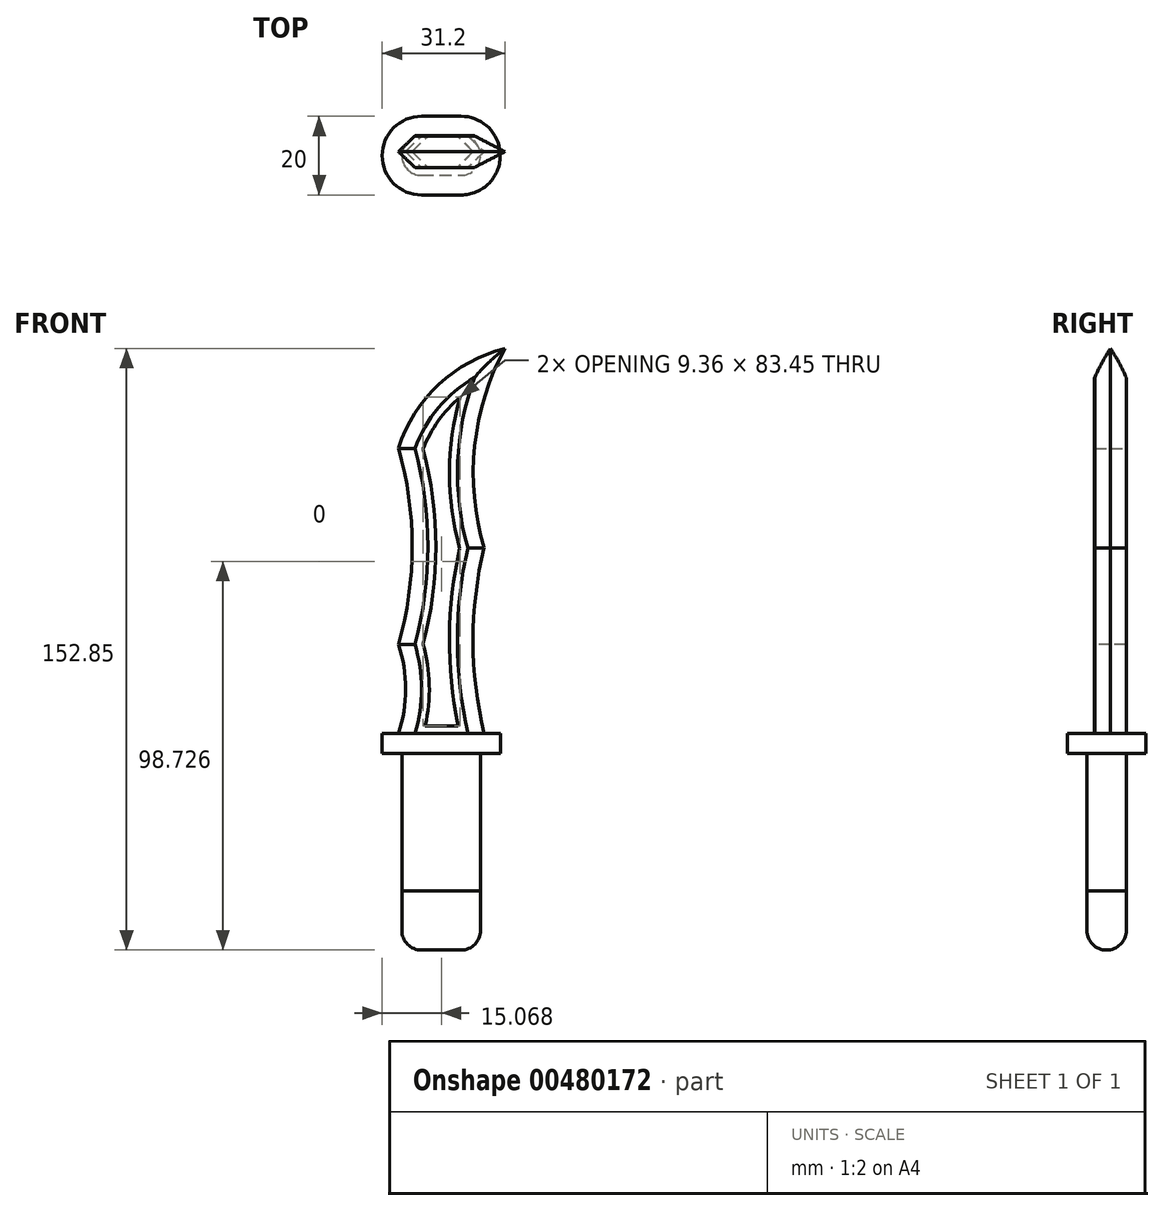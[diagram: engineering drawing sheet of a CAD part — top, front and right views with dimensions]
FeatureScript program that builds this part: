
annotation { "Feature Type Name" : "Feature", "Feature Type Description" : "" }
export const myFeature = defineFeature(function(context is Context, id is Id, definition is map)
    precondition{}
    {
        {
            var Q0;
            Q0=qCreatedBy(makeId("Front.planeOp"),FACE);
            var sketch = newSketch(context, id + "F0", { "sketchPlane" : qUnion([Q0])});
            skLineSegment(sketch, "E0.bottom", {"start": v(-9.92, 0) * mm, "end": v(10.08, 0) * mm});
            skLineSegment(sketch, "E0.top", {"start": v(-9.92, -50) * mm, "end": v(10.08, -50) * mm});
            skLineSegment(sketch, "E0.left", {"start": v(-9.92, 0) * mm, "end": v(-9.92, -50) * mm});
            skLineSegment(sketch, "E0.right", {"start": v(10.08, 0) * mm, "end": v(10.08, -50) * mm});
            skLineSegment(sketch, "E1", {"start": v(-9.92, -35) * mm, "end": v(10.08, -35) * mm});
            skLineSegment(sketch, "E2", {"start": v(-47.28, 5) * mm, "end": v(68.13, 5) * mm});
            skPoint(sketch, "E3", {"position": v(-9.92, 5) * mm});
            skPoint(sketch, "E4", {"position": v(10.08, 5) * mm});
            skPoint(sketch, "E5", {"position": v(14.08, 5) * mm});
            skPoint(sketch, "E6", {"position": v(-13.92, 5) * mm});
            skArc(sketch, "E7", {"start": v(14.08, 52.31) * mm, "mid": v(11.16, 28.66) * mm, "end": v(14.08, 5) * mm});
            skArc(sketch, "E8", {"start": v(22.24, 106.85) * mm, "mid": v(11.9, 80.52) * mm, "end": v(14.08, 52.31) * mm});
            skArc(sketch, "E9", {"start": v(-13.92, 5) * mm, "mid": v(-11.95, 16.28) * mm, "end": v(-13.92, 27.57) * mm});
            skArc(sketch, "E10", {"start": v(-13.92, 27.57) * mm, "mid": v(-10.3, 52.54) * mm, "end": v(-13.92, 77.52) * mm});
            skArc(sketch, "E11", {"start": v(22.24, 106.85) * mm, "mid": v(-0.4, 97.8) * mm, "end": v(-13.92, 77.52) * mm});
            skSolve(sketch);
        }
        {
            var Q0;
            {var subQ0=sQuery(id+"F0.wireOp",EDGE,"E0.bottom");Q0=makeQuery(id+"F0.imprint","IMPRINT",FACE,{"disambiguationData":[TD([[makeQuery(id+"F0.imprint","IMPRINT",EDGE,{"derivedFrom":subQ0}),-1.0]])]});}
            extrude(context, id + "F1", {"entities" : qUnion([Q0]), "depth" : 10 * mm});
        }
        {
            var Q0;
            {var subQ0=sQuery(id+"F0.wireOp",EDGE,"E0.top");Q0=makeQuery(id+"F0.imprint","IMPRINT",FACE,{"disambiguationData":[TD([[makeQuery(id+"F0.imprint","IMPRINT",EDGE,{"derivedFrom":subQ0}),1.0]])]});}
            extrude(context, id + "F2", {"entities" : qUnion([Q0]), "depth" : 10 * mm});
        }
        {
            var Q0;
            Q0=makeQuery(id+"F1.opExtrude","CAP_EDGE",EDGE,{"disambiguationData":[OSD([sQuery(id+"F0.wireOp",EDGE,"E0.right")])],"isStart":false});
            var Q1;
            Q1=makeQuery(id+"F2.opExtrude","CAP_EDGE",EDGE,{"disambiguationData":[OSD([sQuery(id+"F0.wireOp",EDGE,"E0.right")])],"isStart":false});
            var Q2;
            Q2=makeQuery(id+"F1.opExtrude","CAP_EDGE",EDGE,{"disambiguationData":[OSD([sQuery(id+"F0.wireOp",EDGE,"E0.right")])],"isStart":true});
            var Q3;
            Q3=makeQuery(id+"F2.opExtrude","CAP_EDGE",EDGE,{"disambiguationData":[OSD([sQuery(id+"F0.wireOp",EDGE,"E0.right")])],"isStart":true});
            var Q4;
            Q4=makeQuery(id+"F2.opExtrude","CAP_EDGE",EDGE,{"disambiguationData":[OSD([sQuery(id+"F0.wireOp",EDGE,"E0.left")])],"isStart":true});
            var Q5;
            Q5=makeQuery(id+"F1.opExtrude","CAP_EDGE",EDGE,{"disambiguationData":[OSD([sQuery(id+"F0.wireOp",EDGE,"E0.left")])],"isStart":true});
            var Q6;
            Q6=makeQuery(id+"F1.opExtrude","CAP_EDGE",EDGE,{"disambiguationData":[OSD([sQuery(id+"F0.wireOp",EDGE,"E0.left")])],"isStart":false});
            var Q7;
            Q7=makeQuery(id+"F2.opExtrude","CAP_EDGE",EDGE,{"disambiguationData":[OSD([sQuery(id+"F0.wireOp",EDGE,"E0.left")])],"isStart":false});
            var Q8;
            Q8=makeQuery(id+"F2.opExtrude","CAP_EDGE",EDGE,{"disambiguationData":[OSD([sQuery(id+"F0.wireOp",EDGE,"E0.top")])],"isStart":false});
            var Q9;
            Q9=makeQuery(id+"F2.opExtrude","SWEPT_EDGE",EDGE,{"disambiguationData":[OSD([sQuery(id+"F0.wireOp",EDGE,"E0.top"),sQuery(id+"F0.wireOp",EDGE,"E0.left")])]});
            var Q10;
            Q10=makeQuery(id+"F2.opExtrude","CAP_EDGE",EDGE,{"disambiguationData":[OSD([sQuery(id+"F0.wireOp",EDGE,"E0.top")])],"isStart":true});
            var Q11;
            Q11=makeQuery(id+"F2.opExtrude","SWEPT_EDGE",EDGE,{"disambiguationData":[OSD([sQuery(id+"F0.wireOp",EDGE,"E0.top"),sQuery(id+"F0.wireOp",EDGE,"E0.right")])]});
            fillet(context, id + "F3", {"entities" : qUnion([Q0, Q1, Q2, Q3, Q4, Q5, Q6, Q7, Q8, Q9, Q10, Q11]), "radius" : 5 * mm, "tangentPropagation" : true, "allowEdgeOverflow" : false});
        }
        {
            var Q0;
            Q0=qCreatedBy(makeId("Top.planeOp"),FACE);
            var sketch = newSketch(context, id + "F4", { "sketchPlane" : qUnion([Q0])});
            skArc(sketch, "E12.0", {"start": v(5.08, -15) * mm, "mid": v(15.08, -5) * mm, "end": v(5.08, 5) * mm});
            skLineSegment(sketch, "E12.1", {"start": v(-4.92, -15) * mm, "end": v(5.08, -15) * mm});
            skArc(sketch, "E12.2", {"start": v(-4.92, 5) * mm, "mid": v(-14.92, -5) * mm, "end": v(-4.92, -15) * mm});
            skLineSegment(sketch, "E12.3", {"start": v(5.08, 5) * mm, "end": v(-4.92, 5) * mm});
            skSolve(sketch);
        }
        {
            var Q0;
            Q0=makeQuery(id+"F4.imprint","IMPRINT",FACE,{"disambiguationData":[TD([[makeQuery(id+"F4.imprint","IMPRINT",EDGE,{"derivedFrom":sQuery(id+"F4.wireOp",EDGE,"E12.0")}),1.0]])]});
            extrude(context, id + "F5", {"entities" : qUnion([Q0]), "depth" : 5 * mm});
        }
        {
            var Q0;
            {var subQ1=sQuery(id+"F0.wireOp",EDGE,"E7");Q0=makeQuery(id+"F0.imprint","IMPRINT",FACE,{"disambiguationData":[TD([[makeQuery(id+"F0.imprint","IMPRINT",EDGE,{"derivedFrom":subQ1}),-1.0]])]});}
            extrude(context, id + "F6", {"entities" : qUnion([Q0]), "depth" : 8 * mm});
        }
        {
            var Q0;
            Q0=makeQuery(id+"F6.opExtrude","CAP_EDGE",EDGE,{"disambiguationData":[OSD([sQuery(id+"F0.wireOp",EDGE,"E8")])],"isStart":false});
            var Q1;
            Q1=makeQuery(id+"F6.opExtrude","CAP_EDGE",EDGE,{"disambiguationData":[OSD([sQuery(id+"F0.wireOp",EDGE,"E7")])],"isStart":false});
            chamfer(context, id + "F7", {"entities" : qUnion([Q0, Q1]), "width" : 7 * mm, "tangentPropagation" : true});
        }
        {
            var Q0;
            Q0=makeQuery(id+"F6.opExtrude","CAP_EDGE",EDGE,{"disambiguationData":[OSD([sQuery(id+"F0.wireOp",EDGE,"E8")])],"isStart":true});
            var Q1;
            Q1=makeQuery(id+"F6.opExtrude","CAP_EDGE",EDGE,{"disambiguationData":[OSD([sQuery(id+"F0.wireOp",EDGE,"E7")])],"isStart":true});
            chamfer(context, id + "F8", {"entities" : qUnion([Q0, Q1]), "width" : 7 * mm, "tangentPropagation" : true});
        }
        {
            var Q0;
            Q0=makeQuery(id+"F6.opExtrude","CAP_EDGE",EDGE,{"disambiguationData":[OSD([sQuery(id+"F0.wireOp",EDGE,"E11")])],"isStart":true});
            var Q1;
            Q1=makeQuery(id+"F6.opExtrude","CAP_EDGE",EDGE,{"disambiguationData":[OSD([sQuery(id+"F0.wireOp",EDGE,"E10")])],"isStart":true});
            var Q2;
            Q2=makeQuery(id+"F6.opExtrude","CAP_EDGE",EDGE,{"disambiguationData":[OSD([sQuery(id+"F0.wireOp",EDGE,"E9")])],"isStart":true});
            chamfer(context, id + "F9", {"entities" : qUnion([Q0, Q1, Q2]), "width" : 7 * mm, "tangentPropagation" : true});
        }
        {
            var Q0;
            Q0=makeQuery(id+"F6.opExtrude","CAP_EDGE",EDGE,{"disambiguationData":[OSD([sQuery(id+"F0.wireOp",EDGE,"E9")])],"isStart":false});
            var Q1;
            Q1=makeQuery(id+"F6.opExtrude","CAP_EDGE",EDGE,{"disambiguationData":[OSD([sQuery(id+"F0.wireOp",EDGE,"E10")])],"isStart":false});
            var Q2;
            Q2=makeQuery(id+"F6.opExtrude","CAP_EDGE",EDGE,{"disambiguationData":[OSD([sQuery(id+"F0.wireOp",EDGE,"E11")])],"isStart":false});
            chamfer(context, id + "F10", {"entities" : qUnion([Q0, Q1, Q2]), "width" : 7 * mm, "tangentPropagation" : true});
        }
        {
            var Q0;
            Q0=makeQuery(id+"F6.opExtrude","CAP_FACE",FACE,{"disambiguationData":[OSD([sQuery(id+"F0.wireOp",EDGE,"E2"),sQuery(id+"F0.wireOp",EDGE,"E7"),sQuery(id+"F0.wireOp",EDGE,"E8"),sQuery(id+"F0.wireOp",EDGE,"E9"),sQuery(id+"F0.wireOp",EDGE,"E10"),sQuery(id+"F0.wireOp",EDGE,"E11")])],"isStart":false});
            var sketch = newSketch(context, id + "F11", { "sketchPlane" : qUnion([Q0])});
            skArc(sketch, "E13.0", {"start": v(4.39, 7) * mm, "mid": v(2.16, 29.56) * mm, "end": v(4.77, 52.08) * mm});
            skArc(sketch, "E13.1", {"start": v(4.83, 90.45) * mm, "mid": v(-0.69, 84.47) * mm, "end": v(-4.51, 77.29) * mm});
            skArc(sketch, "E13.2", {"start": v(-4.51, 77.29) * mm, "mid": v(-1.3, 52.5) * mm, "end": v(-4.53, 27.73) * mm});
            skArc(sketch, "E13.3", {"start": v(4.77, 52.08) * mm, "mid": v(2.2, 71.27) * mm, "end": v(4.83, 90.45) * mm});
            skArc(sketch, "E13.4", {"start": v(-4.53, 27.73) * mm, "mid": v(-2.96, 17.4) * mm, "end": v(-3.98, 7) * mm});
            skLineSegment(sketch, "E13.5", {"start": v(-3.98, 7) * mm, "end": v(4.39, 7) * mm});
            skSolve(sketch);
        }
        {
            var Q0;
            Q0=makeQuery(id+"F11.imprint","IMPRINT",FACE,{"disambiguationData":[TD([[makeQuery(id+"F11.imprint","IMPRINT",EDGE,{"derivedFrom":sQuery(id+"F11.wireOp",EDGE,"E13.0")}),1.0]])]});
            extrude(context, id + "F12", {"entities" : qUnion([Q0]), "depth" : 0.05 * mm, "offsetDistance" : 25 * mm});
        }
        {
            var Q0;
            Q0=makeQuery(id+"F6.opExtrude","CAP_FACE",FACE,{"disambiguationData":[OSD([sQuery(id+"F0.wireOp",EDGE,"E2"),sQuery(id+"F0.wireOp",EDGE,"E7"),sQuery(id+"F0.wireOp",EDGE,"E8"),sQuery(id+"F0.wireOp",EDGE,"E9"),sQuery(id+"F0.wireOp",EDGE,"E10"),sQuery(id+"F0.wireOp",EDGE,"E11")])],"isStart":true});
            var sketch = newSketch(context, id + "F13", { "sketchPlane" : qUnion([Q0])});
            skArc(sketch, "E14.0", {"start": v(-4.77, 52.08) * mm, "mid": v(-2.16, 29.56) * mm, "end": v(-4.39, 7) * mm});
            skArc(sketch, "E14.1", {"start": v(3.98, 7) * mm, "mid": v(2.96, 17.4) * mm, "end": v(4.53, 27.73) * mm});
            skArc(sketch, "E14.2", {"start": v(4.53, 27.73) * mm, "mid": v(1.3, 52.5) * mm, "end": v(4.51, 77.29) * mm});
            skLineSegment(sketch, "E14.3", {"start": v(-4.39, 7) * mm, "end": v(3.98, 7) * mm});
            skArc(sketch, "E14.4", {"start": v(4.51, 77.29) * mm, "mid": v(0.69, 84.47) * mm, "end": v(-4.83, 90.45) * mm});
            skArc(sketch, "E14.5", {"start": v(-4.83, 90.45) * mm, "mid": v(-2.2, 71.27) * mm, "end": v(-4.77, 52.08) * mm});
            skSolve(sketch);
        }
        {
            var Q0;
            Q0=makeQuery(id+"F13.imprint","IMPRINT",FACE,{"disambiguationData":[TD([[makeQuery(id+"F13.imprint","IMPRINT",EDGE,{"derivedFrom":sQuery(id+"F13.wireOp",EDGE,"E14.0")}),1.0]])]});
            extrude(context, id + "F14", {"entities" : qUnion([Q0]), "depth" : 0.05 * mm});
        }
    });
